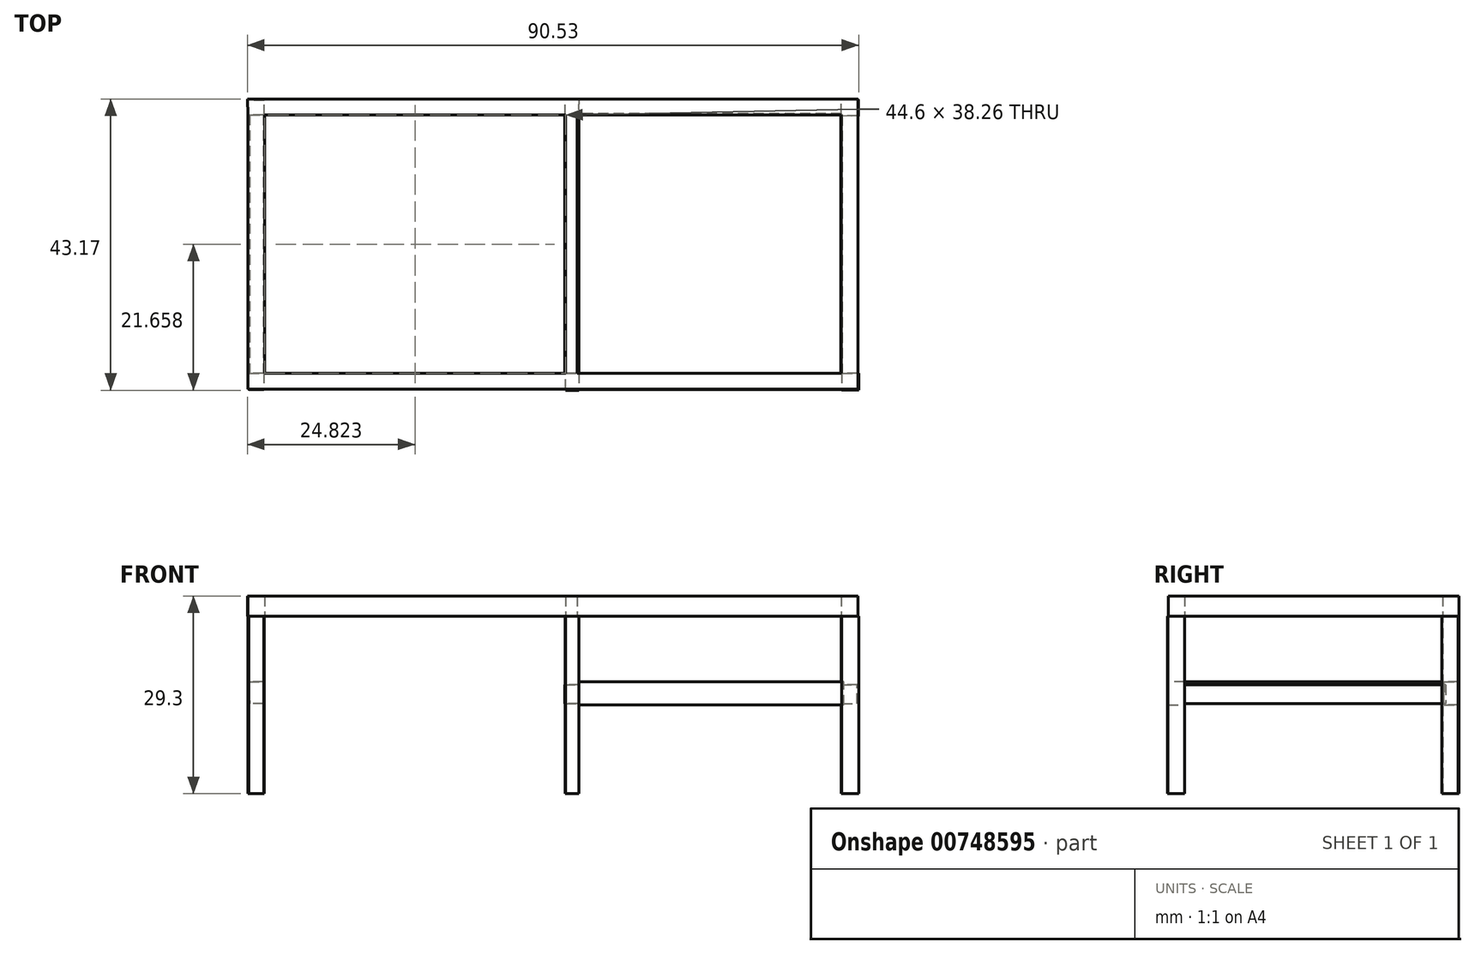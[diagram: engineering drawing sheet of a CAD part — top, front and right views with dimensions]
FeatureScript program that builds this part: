
annotation { "Feature Type Name" : "Feature", "Feature Type Description" : "" }
export const myFeature = defineFeature(function(context is Context, id is Id, definition is map)
    precondition{}
    {
        {
            var Q0;
            Q0=qCreatedBy(makeId("Top.planeOp"),FACE);
            var sketch = newSketch(context, id + "F0", { "sketchPlane" : qUnion([Q0])});
            skLineSegment(sketch, "E0", {"start": v(42.5, 40.63) * mm, "end": v(-47.93, 40.63) * mm});
            skLineSegment(sketch, "E1", {"start": v(42.5, 40.63) * mm, "end": v(42.5, 38.26) * mm});
            skLineSegment(sketch, "E2", {"start": v(40, 38.26) * mm, "end": v(0.91, 38.26) * mm});
            skLineSegment(sketch, "E3", {"start": v(-47.84, 38.26) * mm, "end": v(-47.93, 40.63) * mm});
            skLineSegment(sketch, "E4", {"start": v(-47.84, 38.26) * mm, "end": v(-47.84, 0) * mm});
            skLineSegment(sketch, "E5", {"start": v(42.5, 38.26) * mm, "end": v(42.5, 0) * mm});
            skLineSegment(sketch, "E6", {"start": v(40, 0) * mm, "end": v(40, 38.26) * mm});
            skLineSegment(sketch, "E7", {"start": v(40, 0) * mm, "end": v(0.91, 0) * mm});
            skLineSegment(sketch, "E8", {"start": v(42.5, 0) * mm, "end": v(42.5, -2.39) * mm});
            skLineSegment(sketch, "E9", {"start": v(42.5, -2.39) * mm, "end": v(-47.84, -2.39) * mm});
            skLineSegment(sketch, "E10", {"start": v(-47.84, -2.39) * mm, "end": v(-47.84, 0) * mm});
            skPoint(sketch, "E11.start.orphan", {"position": v(-45.4, 38.26) * mm});
            skPoint(sketch, "E12.orphan", {"position": v(-45.97, 38.26) * mm});
            skLineSegment(sketch, "E13", {"start": v(-45.4, 38.26) * mm, "end": v(-45.4, 0) * mm});
            skLineSegment(sketch, "E14", {"start": v(0.91, 0) * mm, "end": v(0.91, 38.26) * mm});
            skLineSegment(sketch, "E15", {"start": v(-0.81, 38.26) * mm, "end": v(-0.81, 0) * mm});
            skLineSegment(sketch, "E16.trimOffspring", {"start": v(-0.81, 38.26) * mm, "end": v(-45.4, 38.26) * mm});
            skPoint(sketch, "E17.start.orphan", {"position": v(0, 38.26) * mm});
            skLineSegment(sketch, "E18.trimOffspring", {"start": v(-0.81, 0) * mm, "end": v(-45.4, 0) * mm});
            skPoint(sketch, "E19.start.orphan", {"position": v(0, 0) * mm});
            skSolve(sketch);
        }
        {
            var Q0;
            Q0=makeQuery(id+"F0.imprint","IMPRINT",FACE,{"disambiguationData":[TD([[makeQuery(id+"F0.imprint","IMPRINT",EDGE,{"derivedFrom":sQuery(id+"F0.wireOp",EDGE,"E0")}),1.0]])]});
            extrude(context, id + "F1", {"entities" : qUnion([Q0]), "depth" : 3 * mm, "offsetDistance" : 25 * mm});
        }
        {
            var Q0;
            Q0=qCreatedBy(makeId("Top.planeOp"),FACE);
            var sketch = newSketch(context, id + "F2", { "sketchPlane" : qUnion([Q0])});
            skLineSegment(sketch, "E20", {"start": v(40.08, 0) * mm, "end": v(40.08, -2.47) * mm});
            skLineSegment(sketch, "E21", {"start": v(40.08, -2.47) * mm, "end": v(42.6, -2.47) * mm});
            skLineSegment(sketch, "E22", {"start": v(42.6, -2.47) * mm, "end": v(42.6, 0) * mm});
            skLineSegment(sketch, "E23", {"start": v(42.6, 0) * mm, "end": v(40.08, 0) * mm});
            skLineSegment(sketch, "E24", {"start": v(40.03, 38.2) * mm, "end": v(40.03, 40.54) * mm});
            skLineSegment(sketch, "E25", {"start": v(40.03, 40.54) * mm, "end": v(42.56, 40.54) * mm});
            skLineSegment(sketch, "E26", {"start": v(42.56, 40.54) * mm, "end": v(42.56, 38.1) * mm});
            skLineSegment(sketch, "E27", {"start": v(42.56, 38.1) * mm, "end": v(40.03, 38.2) * mm});
            skLineSegment(sketch, "E28", {"start": v(1.16, 0) * mm, "end": v(1.16, -2.53) * mm});
            skLineSegment(sketch, "E29", {"start": v(1.16, -2.53) * mm, "end": v(-0.8, -2.53) * mm});
            skLineSegment(sketch, "E30", {"start": v(-0.8, -2.53) * mm, "end": v(-0.8, 0) * mm});
            skLineSegment(sketch, "E31", {"start": v(-0.8, 0) * mm, "end": v(1.16, 0) * mm});
            skLineSegment(sketch, "E32", {"start": v(1.07, 38.3) * mm, "end": v(-0.9, 38.3) * mm});
            skLineSegment(sketch, "E33", {"start": v(-0.9, 38.3) * mm, "end": v(-0.9, 40.64) * mm});
            skLineSegment(sketch, "E34", {"start": v(-0.9, 40.64) * mm, "end": v(1.16, 40.64) * mm});
            skLineSegment(sketch, "E35", {"start": v(1.16, 40.64) * mm, "end": v(1.07, 38.3) * mm});
            skLineSegment(sketch, "E36", {"start": v(-45.53, 0) * mm, "end": v(-45.53, -2.45) * mm});
            skLineSegment(sketch, "E37", {"start": v(-45.53, -2.45) * mm, "end": v(-47.71, -2.45) * mm});
            skLineSegment(sketch, "E38", {"start": v(-47.71, -2.45) * mm, "end": v(-47.71, 0) * mm});
            skLineSegment(sketch, "E39", {"start": v(-47.71, 0) * mm, "end": v(-45.53, 0) * mm});
            skLineSegment(sketch, "E40", {"start": v(-45.46, 38.27) * mm, "end": v(-45.46, 40.46) * mm});
            skLineSegment(sketch, "E41", {"start": v(-45.46, 40.46) * mm, "end": v(-47.84, 40.46) * mm});
            skLineSegment(sketch, "E42", {"start": v(-45.46, 38.27) * mm, "end": v(-47.84, 38.27) * mm});
            skLineSegment(sketch, "E43", {"start": v(-47.84, 38.27) * mm, "end": v(-47.84, 40.46) * mm});
            skSolve(sketch);
        }
        {
            var Q0;
            Q0 = qSketchRegion(id + "F2", true);
            extrude(context, id + "F3", {"entities" : qUnion([Q0]), "operationType" : NewBodyOperationType.ADD, "oppositeDirection" : true, "depth" : 26.3 * mm, "offsetDistance" : 25 * mm});
        }
        {
            var Q0;
            Q0=qCreatedBy(makeId("Front.planeOp"),FACE);
            var sketch = newSketch(context, id + "F4", { "sketchPlane" : qUnion([Q0])});
            skLineSegment(sketch, "E44", {"start": v(-47.82, -9.7) * mm, "end": v(-45.6, -9.7) * mm});
            skLineSegment(sketch, "E45", {"start": v(-45.6, -9.7) * mm, "end": v(-45.6, -12.93) * mm});
            skLineSegment(sketch, "E46", {"start": v(-45.6, -12.93) * mm, "end": v(-47.6, -12.93) * mm});
            skLineSegment(sketch, "E47", {"start": v(-47.6, -12.93) * mm, "end": v(-47.82, -9.7) * mm});
            skLineSegment(sketch, "E48", {"start": v(-0.93, -12.93) * mm, "end": v(1.18, -12.93) * mm});
            skLineSegment(sketch, "E49", {"start": v(1.18, -12.93) * mm, "end": v(1.18, -10.15) * mm});
            skLineSegment(sketch, "E50", {"start": v(1.18, -10.15) * mm, "end": v(-0.93, -10.15) * mm});
            skLineSegment(sketch, "E51", {"start": v(-0.93, -10.15) * mm, "end": v(-0.93, -12.93) * mm});
            skLineSegment(sketch, "E52", {"start": v(40.16, -12.93) * mm, "end": v(42.39, -12.93) * mm});
            skLineSegment(sketch, "E53", {"start": v(42.39, -12.93) * mm, "end": v(42.39, -10.15) * mm});
            skLineSegment(sketch, "E54", {"start": v(42.39, -10.15) * mm, "end": v(39.94, -10.15) * mm});
            skLineSegment(sketch, "E55", {"start": v(39.94, -10.15) * mm, "end": v(40.16, -12.93) * mm});
            skSolve(sketch);
        }
        {
            var Q0;
            Q0 = qSketchRegion(id + "F4", true);
            extrude(context, id + "F5", {"entities" : qUnion([Q0]), "operationType" : NewBodyOperationType.ADD, "oppositeDirection" : true, "depth" : 38.7 * mm, "offsetDistance" : 25 * mm});
        }
        {
            var Q0;
            Q0=qCreatedBy(makeId("Right.planeOp"),FACE);
            var sketch = newSketch(context, id + "F6", { "sketchPlane" : qUnion([Q0])});
            skLineSegment(sketch, "E56", {"start": v(40.56, -9.7) * mm, "end": v(38.44, -9.7) * mm});
            skLineSegment(sketch, "E57", {"start": v(38.44, -9.7) * mm, "end": v(38.44, -13.15) * mm});
            skLineSegment(sketch, "E58", {"start": v(38.44, -13.15) * mm, "end": v(40.56, -13.15) * mm});
            skLineSegment(sketch, "E59", {"start": v(40.56, -13.15) * mm, "end": v(40.56, -9.7) * mm});
            skLineSegment(sketch, "E60", {"start": v(0, -9.7) * mm, "end": v(-2.43, -9.7) * mm});
            skLineSegment(sketch, "E61", {"start": v(-2.43, -9.7) * mm, "end": v(-2.43, -13.15) * mm});
            skLineSegment(sketch, "E62", {"start": v(-2.43, -13.15) * mm, "end": v(0, -13.15) * mm});
            skLineSegment(sketch, "E63", {"start": v(0, -13.15) * mm, "end": v(0, -9.7) * mm});
            skSolve(sketch);
        }
        {
            var Q0;
            Q0 = qSketchRegion(id + "F6", true);
            extrude(context, id + "F7", {"entities" : qUnion([Q0]), "operationType" : NewBodyOperationType.ADD, "depth" : 40.4 * mm, "offsetDistance" : 25 * mm});
        }
    });
